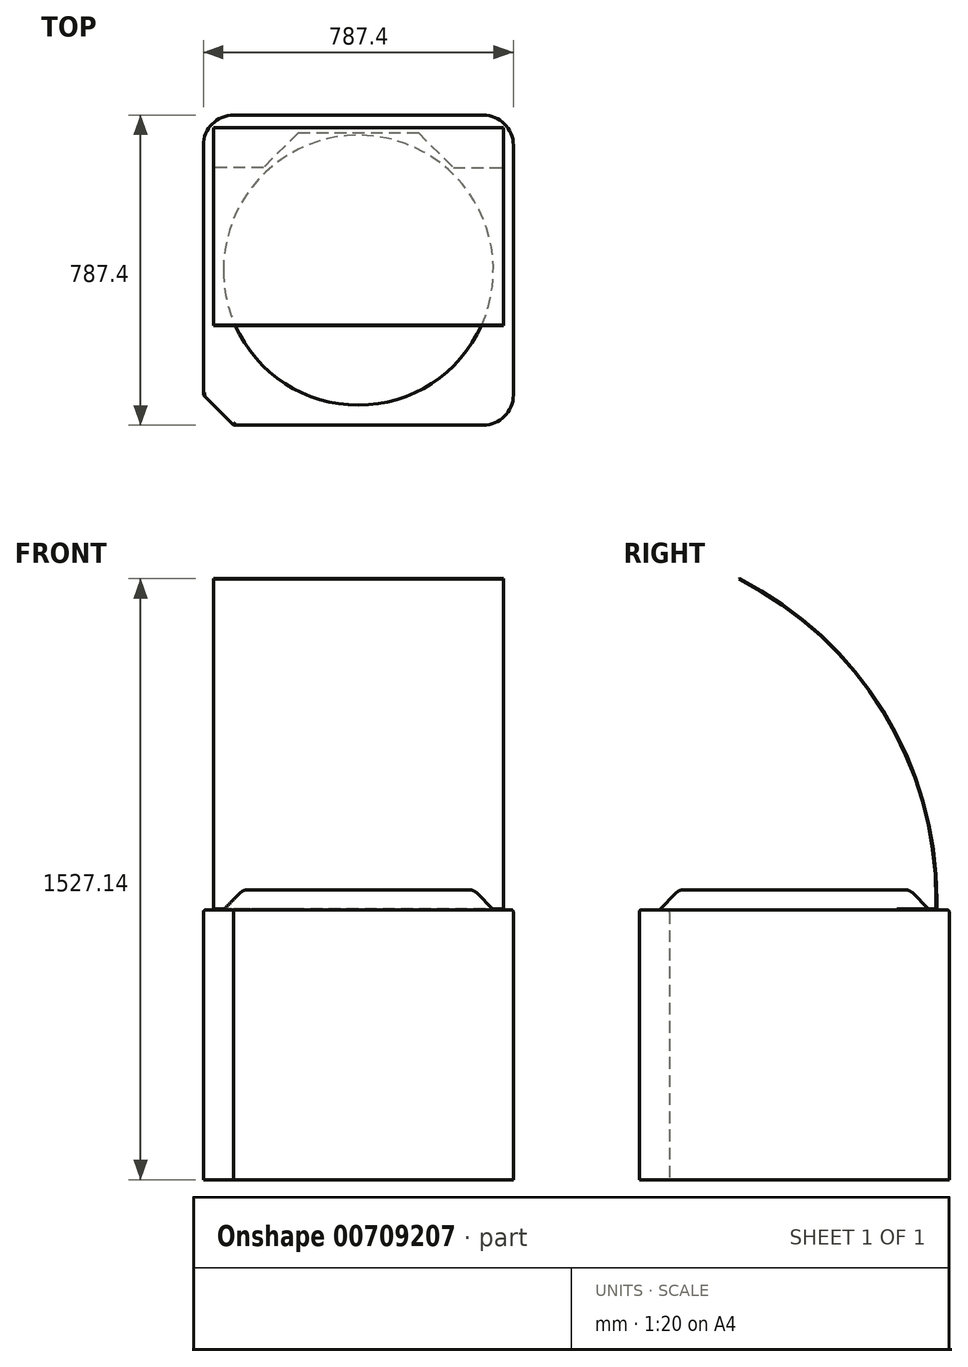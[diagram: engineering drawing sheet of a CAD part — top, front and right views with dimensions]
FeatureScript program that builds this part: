
annotation { "Feature Type Name" : "Feature", "Feature Type Description" : "" }
export const myFeature = defineFeature(function(context is Context, id is Id, definition is map)
    precondition{}
    {
        {
            var Q0;
            Q0=qCreatedBy(makeId("Top.planeOp"),FACE);
            var sketch = newSketch(context, id + "F0", { "sketchPlane" : qUnion([Q0])});
            skLineSegment(sketch, "E0.bottom", {"start": v(317.5, -393.7) * mm, "end": v(-317.5, -393.7) * mm});
            skLineSegment(sketch, "E0.top", {"start": v(317.5, 393.7) * mm, "end": v(-317.5, 393.7) * mm});
            skLineSegment(sketch, "E0.left", {"start": v(393.7, -317.5) * mm, "end": v(393.7, 317.5) * mm});
            skLineSegment(sketch, "E0.right", {"start": v(-393.7, -317.5) * mm, "end": v(-393.7, 317.5) * mm});
            skPoint(sketch, "E0.middle", {"position": v(0, 0) * mm});
            skPoint(sketch, "E1.visualSharp", {"position": v(393.7, 393.7) * mm});
            skArc(sketch, "E1.filletArc", {"start": v(393.7, 317.5) * mm, "mid": v(371.38, 371.38) * mm, "end": v(317.5, 393.7) * mm});
            skPoint(sketch, "E2.visualSharp", {"position": v(-393.7, 393.7) * mm});
            skArc(sketch, "E2.filletArc", {"start": v(-317.5, 393.7) * mm, "mid": v(-371.38, 371.38) * mm, "end": v(-393.7, 317.5) * mm});
            skPoint(sketch, "E3.visualSharp", {"position": v(393.7, -393.7) * mm});
            skArc(sketch, "E3.filletArc", {"start": v(317.5, -393.7) * mm, "mid": v(371.38, -371.38) * mm, "end": v(393.7, -317.5) * mm});
            skLineSegment(sketch, "E4", {"start": v(-393.7, -317.5) * mm, "end": v(-317.5, -393.7) * mm});
            skPoint(sketch, "E5.orphan", {"position": v(-393.7, -393.7) * mm});
            skSolve(sketch);
        }
        {
            var Q0;
            Q0 = qSketchRegion(id + "F0", true);
            extrude(context, id + "F1", {"entities" : qUnion([Q0]), "depth" : 685.8 * mm, "offsetDistance" : 25.4 * mm});
        }
        {
            var Q0;
            Q0=qCreatedBy(makeId("Front.planeOp"),FACE);
            var sketch = newSketch(context, id + "F2", { "sketchPlane" : qUnion([Q0])});
            skLineSegment(sketch, "E6", {"start": v(0, 583.23) * mm, "end": v(0, 787.46) * mm, "construction": true});
            skLineSegment(sketch, "E7", {"start": v(0, 736.6) * mm, "end": v(292.1, 736.6) * mm});
            skLineSegment(sketch, "E8", {"start": v(292.1, 736.6) * mm, "end": v(342.9, 685.8) * mm});
            skLineSegment(sketch, "E9", {"start": v(342.9, 685.8) * mm, "end": v(0, 685.8) * mm});
            skLineSegment(sketch, "E10", {"start": v(0, 685.8) * mm, "end": v(0, 736.6) * mm});
            skSolve(sketch);
        }
        {
            var Q0;
            Q0 = qSketchRegion(id + "F2", true);
            var Q1;
            Q1=sQuery(id+"F2.wireOp",EDGE,"E6");
            revolve(context, id + "F3", {"operationType" : NewBodyOperationType.ADD, "surfaceOperationType" : NewSurfaceOperationType.NEW, "entities" : qUnion([Q0]), "axis" : qUnion([Q1]), "revolveType" : RevolveType.FULL});
        }
        {
            var Q0;
            Q0=makeQuery(id+"F1.opExtrude","CAP_EDGE",EDGE,{"disambiguationData":[OSD([sQuery(id+"F0.wireOp",EDGE,"E3.filletArc")])],"isStart":false});
            var Q1;
            Q1=makeQuery(id+"F1.opExtrude","CAP_EDGE",EDGE,{"disambiguationData":[OSD([sQuery(id+"F0.wireOp",EDGE,"E4")])],"isStart":false});
            fillet(context, id + "F4", {"entities" : qUnion([Q0, Q1]), "radius" : 6.35 * mm, "tangentPropagation" : true, "allowEdgeOverflow" : false});
        }
        {
            var Q0;
            Q0=makeQuery(id+"F3.opRevolve","SWEPT_EDGE",EDGE,{"disambiguationData":[OSD([sQuery(id+"F2.wireOp",EDGE,"E7"),sQuery(id+"F2.wireOp",EDGE,"E8")])]});
            fillet(context, id + "F5", {"entities" : qUnion([Q0]), "radius" : 25.4 * mm, "tangentPropagation" : true, "allowEdgeOverflow" : false});
        }
        {
            var Q0;
            Q0=makeQuery(id+"F1.opExtrude","CAP_FACE",FACE,{"disambiguationData":[OSD([sQuery(id+"F0.wireOp",EDGE,"E0.bottom"),sQuery(id+"F0.wireOp",EDGE,"E0.top"),sQuery(id+"F0.wireOp",EDGE,"E0.left"),sQuery(id+"F0.wireOp",EDGE,"E0.right"),sQuery(id+"F0.wireOp",EDGE,"E1.filletArc"),sQuery(id+"F0.wireOp",EDGE,"E2.filletArc"),sQuery(id+"F0.wireOp",EDGE,"E3.filletArc"),sQuery(id+"F0.wireOp",EDGE,"E4")])],"isStart":false});
            var sketch = newSketch(context, id + "F6", { "sketchPlane" : qUnion([Q0])});
            skLineSegment(sketch, "E11", {"start": v(0, 0) * mm, "end": v(0, 168.04) * mm, "construction": true});
            skLineSegment(sketch, "E12", {"start": v(241.3, 260.35) * mm, "end": v(368.3, 260.35) * mm});
            skLineSegment(sketch, "E13", {"start": v(368.3, 260.35) * mm, "end": v(368.3, 361.95) * mm});
            skLineSegment(sketch, "E14", {"start": v(368.3, 361.95) * mm, "end": v(-368.3, 361.95) * mm});
            skLineSegment(sketch, "E15", {"start": v(-241.3, 260.35) * mm, "end": v(-368.3, 260.35) * mm});
            skLineSegment(sketch, "E16", {"start": v(-368.3, 260.35) * mm, "end": v(-368.3, 361.95) * mm});
            skLineSegment(sketch, "E17", {"start": v(-152.4, 349.25) * mm, "end": v(152.4, 349.25) * mm});
            skLineSegment(sketch, "E18", {"start": v(152.4, 349.25) * mm, "end": v(241.3, 260.35) * mm});
            skLineSegment(sketch, "E19", {"start": v(-152.4, 349.25) * mm, "end": v(-241.3, 260.35) * mm});
            skPoint(sketch, "E20", {"position": v(0, 342.9) * mm});
            skPoint(sketch, "E20.positionSnap0", {"position": v(0, 361.95) * mm});
            skSolve(sketch);
        }
        {
            var Q0;
            Q0 = qSketchRegion(id + "F6", true);
            extrude(context, id + "F7", {"entities" : qUnion([Q0]), "depth" : 1.57 * mm, "offsetDistance" : 25.4 * mm});
        }
        {
            var Q0;
            Q0=qCreatedBy(makeId("Right.planeOp"),FACE);
            var sketch = newSketch(context, id + "F8", { "sketchPlane" : qUnion([Q0])});
            skLineSegment(sketch, "E21", {"start": v(361.95, 685.8) * mm, "end": v(361.95, 711.2) * mm});
            skArc(sketch, "E22", {"start": v(361.95, 711.2) * mm, "mid": v(226.5, 1190.1) * mm, "end": v(-139.7, 1527.14) * mm});
            skArc(sketch, "E23.0", {"start": v(360.38, 711.2) * mm, "mid": v(225.16, 1189.28) * mm, "end": v(-140.41, 1525.74) * mm});
            skLineSegment(sketch, "E24", {"start": v(-139.7, 1527.14) * mm, "end": v(-140.41, 1525.74) * mm});
            skLineSegment(sketch, "E25", {"start": v(360.38, 711.2) * mm, "end": v(360.38, 685.8) * mm});
            skLineSegment(sketch, "E26", {"start": v(360.38, 685.8) * mm, "end": v(361.95, 685.8) * mm});
            skSolve(sketch);
        }
        {
            var Q0;
            Q0 = qSketchRegion(id + "F8", true);
            extrude(context, id + "F9", {"entities" : qUnion([Q0]), "operationType" : NewBodyOperationType.ADD, "depth" : 368.3 * mm, "offsetDistance" : 25.4 * mm, "hasSecondDirection" : true, "secondDirectionOppositeDirection" : true, "secondDirectionDepth" : 368.3 * mm});
        }
    });
